# Revit family: Roof_Drain-Jay R. Smith-Round_Type-1910_Series
name_source: partatom
category: Plumbing Fixtures
units: mm (PartAtom-declared; Revit-internal decimal feet)

## family parameters
Always vertical = Yes
Cut with Voids When Loaded = No
OmniClass Number = 23.70.50.21.24.11
OmniClass Title = Roof Waste Water Drains
Part Type = Normal
Room Calculation Point = No
Round Connector Dimension = Use Diameter
Shared = No
Work Plane-Based = Yes

## types (15) — shared parameters
Assembly Code = D2040200
Body Material = Cast Iron-Jay R Smith-Duco Coated
C - Underdeck Clamp = No
CW Connection = No
Default Elevation = 0"
Description = Roof Drain with Standpipe, Large Area Planter Type
Diameter = 12"
Dome Height = 4 1/2"
Dome Material = Metal-Jay R. Smith-Bronze
HW Connection = No
Installation Type = Roof Mounted
Manufacturer = Jay R. Smith Mfg. Co.
Material = Cast Iron-Jay R Smith-Duco Coated
Product Documentation Link = https://www.jrsmith.com
Product Page URL = https://www.jrsmith.com
R - Sump Receiver = No
Standpipe Cover Material = Metal-Jay R. Smith-Bronze
Standpipe Longer (When Specified) = No
Standpipe Material = Metal-Jay R. Smith-Bronze
U - Vandal Proof Dome = No
URL = http://www.jrsmith.com
Vent Connection = No
Waste Connection = Yes

## per-type parameters (varying)
| type | Bottom Depth | Connection Outlet Description | Connection Radius | Connection Size |
| 1910Y02 | 6" | 2" No-HUB Outlet Connection | 1" | 2" |
| 1910Y03 | 6" | 3" No-HUB Outlet Connection | 1 1/2" | 3" |
| 1910Y04 | 6" | 4" No-HUB Outlet Connection | 2" | 4" |
| 1910Y05 | 6" | 5" No-HUB Outlet Connection | 2 1/2" | 5" |
| 1910Y06 | 6" | 6" No-HUB Outlet Connection | 3" | 6" |
| 1910C02 | 6" | 2" Caulk Outlet Connection | 1" | 2" |
| 1910C03 | 6" | 3" Caulk Outlet Connection | 1 1/2" | 3" |
| 1910C04 | 6" | 4" Caulk Outlet Connection | 2" | 4" |
| 1910C05 | 6" | 5" Caulk Outlet Connection | 2 1/2" | 5" |
| 1910C06 | 6" | 6" Caulk Outlet Connection | 3" | 6" |
| 1910T02 | 4 3/4" | 2" Threaded Outlet Connection | 1" | 2" |
| 1910T03 | 4 3/4" | 3" Threaded Outlet Connection | 1 1/2" | 3" |
| 1910T04 | 4 3/4" | 4" Threaded Outlet Connection | 2" | 4" |
| 1910T05 | 4 3/4" | 5" Threaded Outlet Connection | 2 1/2" | 5" |
| 1910T06 | 4 3/4" | 6" Threaded Outlet Connection | 3" | 6" |

note: column(s) folded — value = type name in every type: Model

## geometry (parser evidence)
native form markers: Sweep x7
no freeform markers — native parametric forms only
